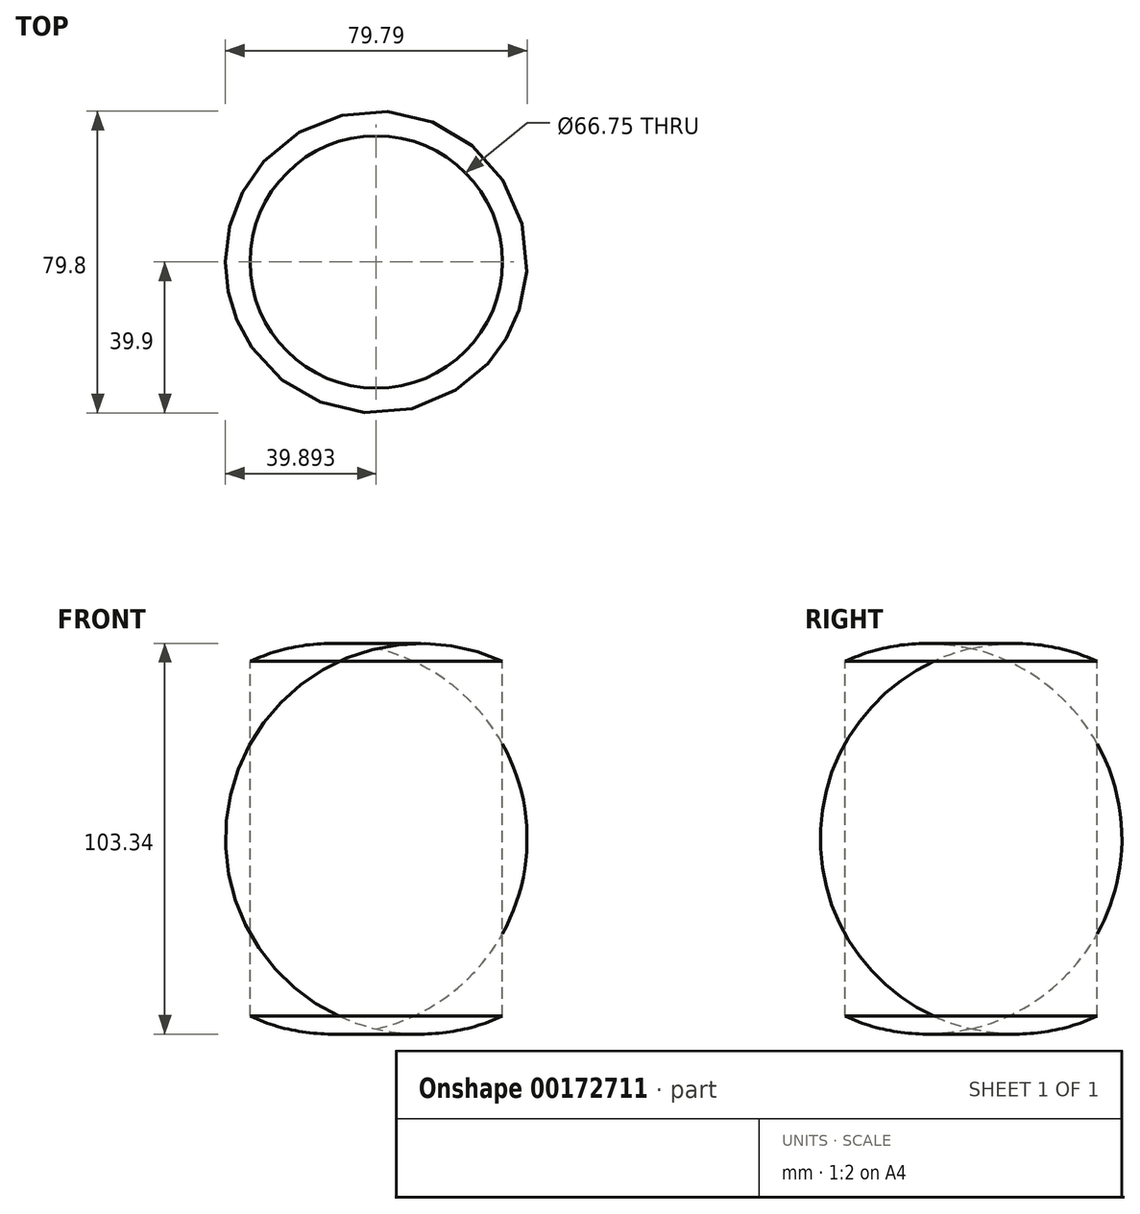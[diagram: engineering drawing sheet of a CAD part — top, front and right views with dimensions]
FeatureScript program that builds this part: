
annotation { "Feature Type Name" : "Feature", "Feature Type Description" : "" }
export const myFeature = defineFeature(function(context is Context, id is Id, definition is map)
    precondition{}
    {
        {
            var Q0;
            Q0=qCreatedBy(makeId("Front.planeOp"),FACE);
            var sketch = newSketch(context, id + "F0", { "sketchPlane" : qUnion([Q0])});
            skLineSegment(sketch, "E0", {"start": v(-44.85, 54.08) * mm, "end": v(-44.85, -38) * mm});
            skLineSegment(sketch, "E1", {"start": v(-11.47, 55.87) * mm, "end": v(-11.47, -38) * mm});
            skArc(sketch, "E2", {"start": v(-11.47, -38) * mm, "mid": v(18.6, 8.94) * mm, "end": v(-11.47, 55.87) * mm});
            skSolve(sketch);
        }
        {
            var Q0;
            Q0=makeQuery(id+"F0.imprint","IMPRINT",FACE,{"disambiguationData":[TD([[makeQuery(id+"F0.imprint","IMPRINT",EDGE,{"derivedFrom":sQuery(id+"F0.wireOp",EDGE,"E1")}),1.0]])]});
            var Q1;
            Q1=sQuery(id+"F0.wireOp",EDGE,"E0");
            revolve(context, id + "F1", {"entities" : qUnion([Q0]), "axis" : qUnion([Q1]), "revolveType" : RevolveType.FULL});
        }
    });
